# Revit family: Towel Rail-Single-Dorf Motif
name_source: partatom
category: Specialty Equipment
revit_build: Autodesk Revit 2013 (Build: 20121003_2115(x64)
units: mm (PartAtom-declared; Revit-internal decimal feet)

## types (3) — shared parameters
Assembly Code = C1030200
Default Elevation = 900 mm  [stored 2.95276 ft]
Manufacturer = GWA Bathrooms & Kitchens
Material_ANZRS = Metal-Chrome-Caroma
ModifiedIssue_ANZRS = 2013.1 $
URL = http://www.dorf.com.au
zero-valued in all types: Cost

## per-type parameters (varying)
| type | Length_ANZRS | Model | Size | Type Comments |
| Single Towel Rail-180mm | 161 mm | 2389.04 | 1 | Dorf Motif Single Towel Rail 180mm |
| Single Towel Rail-350mm | 331 mm | 2390.04 | 2 | Dorf Motif Single Towel Rail 350mm |
| Single Towel Rail-700mm | 681 mm | 2391.04 | 3 | Dorf Motif Single Towel Rail 700mm |

note: [stored X ft] marks values corroborated as IEEE doubles in the binary element streams (Revit-internal decimal feet)

## geometry (parser evidence)
native form markers: Blend x8, Sweep x1
no freeform markers — native parametric forms only
